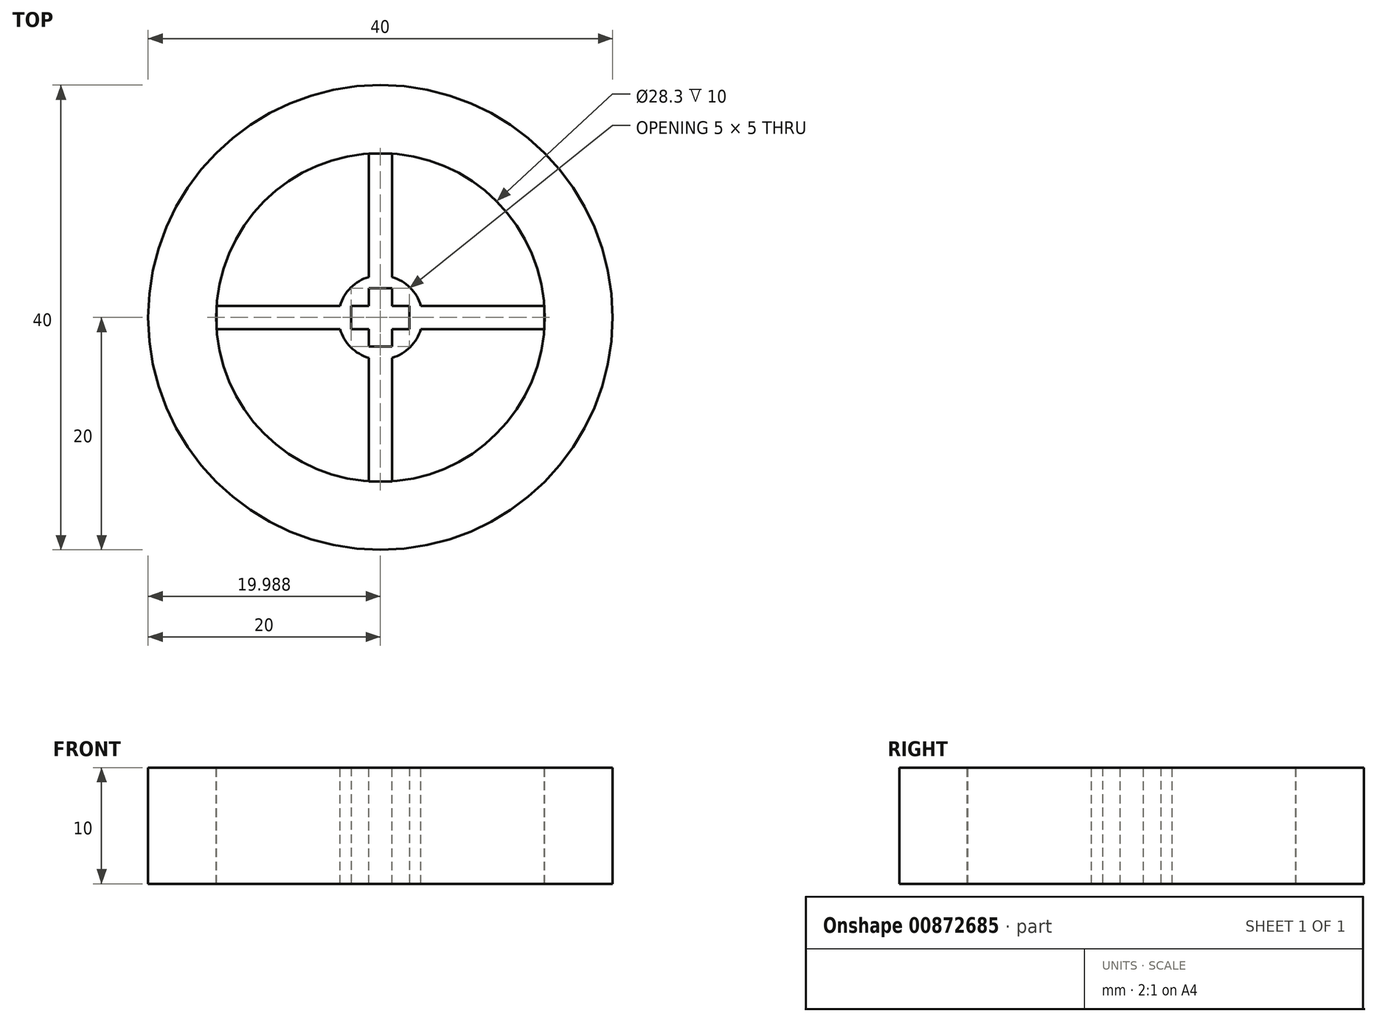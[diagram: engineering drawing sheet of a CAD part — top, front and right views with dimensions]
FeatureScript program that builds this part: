
annotation { "Feature Type Name" : "Feature", "Feature Type Description" : "" }
export const myFeature = defineFeature(function(context is Context, id is Id, definition is map)
    precondition{}
    {
        {
            var Q0;
            Q0=qCreatedBy(makeId("Top.planeOp"),FACE);
            var sketch = newSketch(context, id + "F0", { "sketchPlane" : qUnion([Q0])});
            skLineSegment(sketch, "E0.bottom", {"start": v(-2.51, 1) * mm, "end": v(2.49, 1) * mm});
            skLineSegment(sketch, "E0.top", {"start": v(-2.51, -1) * mm, "end": v(2.49, -1) * mm});
            skLineSegment(sketch, "E0.left", {"start": v(-2.51, 1) * mm, "end": v(-2.51, -1) * mm});
            skLineSegment(sketch, "E0.right", {"start": v(2.49, 1) * mm, "end": v(2.49, -1) * mm});
            skLineSegment(sketch, "E1.bottom", {"start": v(-0.99, 2.5) * mm, "end": v(1.01, 2.5) * mm});
            skLineSegment(sketch, "E1.top", {"start": v(-0.99, -2.5) * mm, "end": v(1.01, -2.5) * mm});
            skLineSegment(sketch, "E1.left", {"start": v(-0.99, 2.5) * mm, "end": v(-0.99, -2.5) * mm});
            skLineSegment(sketch, "E1.right", {"start": v(1.01, 2.5) * mm, "end": v(1.01, -2.5) * mm});
            skSolve(sketch);
        }
        {
            var Q0;
            Q0=qCreatedBy(makeId("Top.planeOp"),FACE);
            var sketch = newSketch(context, id + "F1", { "sketchPlane" : qUnion([Q0])});
            skCircle(sketch, "E2", {"center": v(0, 0) * mm, "radius": 3.62 * mm});
            skSolve(sketch);
        }
        {
            var Q0;
            Q0=makeQuery(id+"F1.imprint","IMPRINT",FACE,{"disambiguationData":[TD([[makeQuery(id+"F1.imprint","IMPRINT",EDGE,{"derivedFrom":sQuery(id+"F1.wireOp",EDGE,"E2")}),1.0]])]});
            extrude(context, id + "F2", {"entities" : qUnion([Q0]), "depth" : 10 * mm, "offsetDistance" : 25 * mm});
        }
        {
            var Q0;
            {var subQ0=sQuery(id+"F0.wireOp",EDGE,"E1.left");var subQ1=sQuery(id+"F0.wireOp",EDGE,"E0.bottom");var subQ2=makeQuery(id+"F0.imprint","INTERSECT",VERTEX,{"derivedFrom":[subQ1,subQ0]});Q0=makeQuery(id+"F0.imprint","IMPRINT",FACE,{"disambiguationData":[TD([[makeQuery(id+"F0.imprint","IMPRINT",EDGE,{"disambiguationData":[TD([[subQ2,-1.0]])],"derivedFrom":subQ1}),-1.0]])]});}
            var Q1;
            {var subQ0=sQuery(id+"F0.wireOp",EDGE,"E0.right");Q1=makeQuery(id+"F0.imprint","IMPRINT",FACE,{"disambiguationData":[TD([[makeQuery(id+"F0.imprint","IMPRINT",EDGE,{"derivedFrom":subQ0}),-1.0]])]});}
            var Q2;
            {var subQ5=sQuery(id+"F0.wireOp",EDGE,"E1.top");Q2=makeQuery(id+"F0.imprint","IMPRINT",FACE,{"disambiguationData":[TD([[makeQuery(id+"F0.imprint","IMPRINT",EDGE,{"derivedFrom":subQ5}),1.0]])]});}
            var Q3;
            {var subQ5=sQuery(id+"F0.wireOp",EDGE,"E1.bottom");Q3=makeQuery(id+"F0.imprint","IMPRINT",FACE,{"disambiguationData":[TD([[makeQuery(id+"F0.imprint","IMPRINT",EDGE,{"derivedFrom":subQ5}),-1.0]])]});}
            var Q4;
            {var subQ0=sQuery(id+"F0.wireOp",EDGE,"E0.left");Q4=makeQuery(id+"F0.imprint","IMPRINT",FACE,{"disambiguationData":[TD([[makeQuery(id+"F0.imprint","IMPRINT",EDGE,{"derivedFrom":subQ0}),1.0]])]});}
            var Q5;
            Q5=qSketchRegion(id+"F3iHN0mLzB50SuE_2",true);
            extrude(context, id + "F3", {"entities" : qUnion([Q0, Q1, Q2, Q3, Q4, Q5]), "operationType" : NewBodyOperationType.REMOVE, "depth" : 10 * mm, "offsetDistance" : 25 * mm});
        }
        {
            var Q0;
            Q0=makeQuery(id+"F2.opExtrude","CAP_FACE",FACE,{"disambiguationData":[OSD([sQuery(id+"F1.wireOp",EDGE,"E2")])],"isStart":false});
            var sketch = newSketch(context, id + "F4", { "sketchPlane" : qUnion([Q0])});
            skCircle(sketch, "E3", {"center": v(0, 0) * mm, "radius": 20 * mm});
            skCircle(sketch, "E4", {"center": v(0, 0) * mm, "radius": 14.15 * mm});
            skLineSegment(sketch, "E5", {"start": v(-0.99, -2.5) * mm, "end": v(-0.99, -14.11) * mm});
            skLineSegment(sketch, "E6", {"start": v(1.01, -2.5) * mm, "end": v(1.01, -14.11) * mm});
            skLineSegment(sketch, "E7", {"start": v(1.01, -14.11) * mm, "end": v(-0.99, -14.11) * mm});
            skLineSegment(sketch, "E8", {"start": v(2.49, 1) * mm, "end": v(14.11, 1) * mm});
            skLineSegment(sketch, "E9", {"start": v(2.49, -1) * mm, "end": v(14.11, -1) * mm});
            skLineSegment(sketch, "E10", {"start": v(14.11, -1) * mm, "end": v(14.11, 1) * mm});
            skLineSegment(sketch, "E11", {"start": v(1.01, 2.5) * mm, "end": v(1.01, 14.11) * mm});
            skLineSegment(sketch, "E12", {"start": v(-0.99, 2.5) * mm, "end": v(-0.99, 14.11) * mm});
            skLineSegment(sketch, "E13", {"start": v(-0.99, 14.11) * mm, "end": v(1.01, 14.11) * mm});
            skLineSegment(sketch, "E14", {"start": v(-2.51, 1) * mm, "end": v(-14.11, 1) * mm});
            skLineSegment(sketch, "E15", {"start": v(-2.51, -1) * mm, "end": v(-14.11, -1) * mm});
            skLineSegment(sketch, "E16", {"start": v(-14.11, -1) * mm, "end": v(-14.11, 1) * mm});
            skSolve(sketch);
        }
        {
            var Q0;
            {var subQ0=sQuery(id+"F4.wireOp",EDGE,"E13");Q0=makeQuery(id+"F4.imprint","IMPRINT",FACE,{"disambiguationData":[TD([[makeQuery(id+"F4.imprint","IMPRINT",EDGE,{"derivedFrom":subQ0}),-1.0]])]});}
            var Q1;
            {var subQ0=sQuery(id+"F4.wireOp",EDGE,"E10");Q1=makeQuery(id+"F4.imprint","IMPRINT",FACE,{"disambiguationData":[TD([[makeQuery(id+"F4.imprint","IMPRINT",EDGE,{"derivedFrom":subQ0}),1.0]])]});}
            var Q2;
            {var subQ0=sQuery(id+"F4.wireOp",EDGE,"E7");Q2=makeQuery(id+"F4.imprint","IMPRINT",FACE,{"disambiguationData":[TD([[makeQuery(id+"F4.imprint","IMPRINT",EDGE,{"derivedFrom":subQ0}),-1.0]])]});}
            var Q3;
            {var subQ0=sQuery(id+"F4.wireOp",EDGE,"E16");Q3=makeQuery(id+"F4.imprint","IMPRINT",FACE,{"disambiguationData":[TD([[makeQuery(id+"F4.imprint","IMPRINT",EDGE,{"derivedFrom":subQ0}),-1.0]])]});}
            var Q4;
            Q4=makeQuery(id+"F4.imprint","IMPRINT",FACE,{"disambiguationData":[TD([[makeQuery(id+"F4.imprint","IMPRINT",EDGE,{"derivedFrom":sQuery(id+"F4.wireOp",EDGE,"E3")}),1.0]])]});
            extrude(context, id + "F5", {"entities" : qUnion([Q0, Q1, Q2, Q3, Q4]), "operationType" : NewBodyOperationType.ADD, "oppositeDirection" : true, "depth" : 10 * mm, "offsetDistance" : 25 * mm});
        }
    });
